# Revit family: Door-Exterior_Interior-Simpson-Sash-Three_Quarter-Half_Arch_Glass-Single
name_source: partatom
category: Doors
revit_build: Autodesk Revit Architecture 2012 (Build: 20110916_2132(x64)
units: mm (PartAtom-declared; Revit-internal decimal feet)

## types (231) — shared parameters
Assembly Code = B2030230
Bottom Panel Height = 0' - 11 5/8"
Bottom Rail Height = 0' - 8 13/16"
Construction Type = Wood
Frame = Wood - Simpson Doors - Douglas Fir
Frame Projection Ext. = 0' - 1"
Frame Projection Int. = 0' - 1"
Frame Type = Frame : Standard
Frame Width = 0' - 3"
Function = Exterior
Glass = Glass - Simpson Doors - Clear
Glass Options = http://simpsondoor.com
Horizontal Outside Muntin = No
Innerbond Double Hip-Raised Panel = Yes
Manufacturer = Simpsons Door Company
Middle Rail Height = 0' - 6 1/2"
Muntin Width = 0' - 0 1/2"
Ovolo Construction = Yes
Panel = Wood - Simpson Doors - Douglas Fir
Panel Divider Width = 0' - 3 1/2"
Panel Stile Width = 0' - 5"
Product Documentation Link = http://www.simpsondoor.com
Product Page URL = http://www.simpsondoor.com
Thickness = 0' - 1 3/4"
Thickness Note = comes in 1 3/4" and 2 1/4" Thickness. Default is set to 1 3/4"
Top Rail Height = 0' - 4 1/32"
URL = http://www.simpsondoor.com
UltraBlock Note = This Door Comes with The Option of UltraBlock Technology. It is Turn On as a Default
UltraBlock Option = Yes
Vertical Outside Muntin = No
Wall Closure = By host
WaterBarrier Note = This Door Comes with The Option of WaterBarrier with UltraBlock Technology. It is Turn Off as a Default
WaterBarrier with UltraBlock Technology = No
Wood Species = http://simpsondoor.com
Wood Species Note = Available in Any Wood Species
zero-valued in all types: Number of Panel Dividers

## per-type parameters (varying)
| type | Description | Height | Model | Number of Horizontal Muntins | Number of Vertical Muntins | Rough Height | Rough Width | Width |
| 37604-37614 Thermal French 30x80 Ovolo Flat Panel | Thermal French SDL - Four Lite - Single Panel | 6' - 8" | 37604-37614 | 1 | 1 | 6' - 10" | 2' - 10" | 2' - 6" |
| 37604-37614 Thermal French 30x84 Ovolo Flat Panel | Thermal French SDL - Four Lite - Single Panel | 7' - 0" | 37604-37614 | 1 | 1 | 7' - 2" | 2' - 10" | 2' - 6" |
| 37604-37614 Thermal French 30x96 Ovolo Flat Panel | Thermal French SDL - Four Lite - Single Panel | 8' - 0" | 37604-37614 | 1 | 1 | 8' - 2" | 2' - 10" | 2' - 6" |
| 37604-37614 Thermal French 32x80 Ovolo Flat Panel | Thermal French SDL - Four Lite - Single Panel | 6' - 8" | 37604-37614 | 1 | 1 | 6' - 10" | 3' - 0" | 2' - 8" |
| 37604-37614 Thermal French 32x84 Ovolo Flat Panel | Thermal French SDL - Four Lite - Single Panel | 7' - 0" | 37604-37614 | 1 | 1 | 7' - 2" | 3' - 0" | 2' - 8" |
| 37604-37614 Thermal French 32x96 Ovolo Flat Panel | Thermal French SDL - Four Lite - Single Panel | 8' - 0" | 37604-37614 | 1 | 1 | 8' - 2" | 3' - 0" | 2' - 8" |
| 37604-37614 Thermal French 34x80 Ovolo Flat Panel | Thermal French SDL - Four Lite - Single Panel | 6' - 8" | 37604-37614 | 1 | 1 | 6' - 10" | 3' - 2" | 2' - 10" |
| 37604-37614 Thermal French 34x84 Ovolo Flat Panel | Thermal French SDL - Four Lite - Single Panel | 7' - 0" | 37604-37614 | 1 | 1 | 7' - 2" | 3' - 2" | 2' - 10" |
| 37604-37614 Thermal French 34x96 Ovolo Flat Panel | Thermal French SDL - Four Lite - Single Panel | 8' - 0" | 37604-37614 | 1 | 1 | 8' - 2" | 3' - 2" | 2' - 10" |
| 37604-37614 Thermal French 36x80 Ovolo Flat Panel | Thermal French SDL - Four Lite - Single Panel | 6' - 8" | 37604-37614 | 1 | 1 | 6' - 10" | 3' - 4" | 3' - 0" |
| 37604-37614 Thermal French 36x84 Ovolo Flat Panel | Thermal French SDL - Four Lite - Single Panel | 7' - 0" | 37604-37614 | 1 | 1 | 7' - 2" | 3' - 4" | 3' - 0" |
| 37604-37614 Thermal French 36x96 Ovolo Flat Panel | Thermal French SDL - Four Lite - Single Panel | 8' - 0" | 37604-37614 | 1 | 1 | 8' - 2" | 3' - 4" | 3' - 0" |
| 37604-37614 Thermal French 38x80 Ovolo Flat Panel | Thermal French SDL - Four Lite - Single Panel | 6' - 8" | 37604-37614 | 1 | 1 | 6' - 10" | 3' - 6" | 3' - 2" |
| 37604-37614 Thermal French 38x84 Ovolo Flat Panel | Thermal French SDL - Four Lite - Single Panel | 7' - 0" | 37604-37614 | 1 | 1 | 7' - 2" | 3' - 6" | 3' - 2" |
| 37604-37614 Thermal French 38x96 Ovolo Flat Panel | Thermal French SDL - Four Lite - Single Panel | 8' - 0" | 37604-37614 | 1 | 1 | 8' - 2" | 3' - 6" | 3' - 2" |
| 37604-37614 Thermal French 40x80 Ovolo Flat Panel | Thermal French SDL - Four Lite - Single Panel | 6' - 8" | 37604-37614 | 1 | 1 | 6' - 10" | 3' - 8" | 3' - 4" |
| 37604-37614 Thermal French 40x84 Ovolo Flat Panel | Thermal French SDL - Four Lite - Single Panel | 7' - 0" | 37604-37614 | 1 | 1 | 7' - 2" | 3' - 8" | 3' - 4" |
| 37604-37614 Thermal French 40x96 Ovolo Flat Panel | Thermal French SDL - Four Lite - Single Panel | 8' - 0" | 37604-37614 | 1 | 1 | 8' - 2" | 3' - 8" | 3' - 4" |
| 37604-37614 Thermal French 42x80 Ovolo Flat Panel | Thermal French SDL - Four Lite - Single Panel | 6' - 8" | 37604-37614 | 1 | 1 | 6' - 10" | 3' - 10" | 3' - 6" |
| 37604-37614 Thermal French 42x84 Ovolo Flat Panel | Thermal French SDL - Four Lite - Single Panel | 7' - 0" | 37604-37614 | 1 | 1 | 7' - 2" | 3' - 10" | 3' - 6" |
| 37604-37614 Thermal French 42x96 Ovolo Flat Panel | Thermal French SDL - Four Lite - Single Panel | 8' - 0" | 37604-37614 | 1 | 1 | 8' - 2" | 3' - 10" | 3' - 6" |
| 37626-37636 Thermal French 30x80 Ovolo Flat Panel | Thermal French SDL - Six Lite - Single Panel | 6' - 8" | 37626-37636 | 2 | 1 | 6' - 10" | 2' - 10" | 2' - 6" |
| 37626-37636 Thermal French 30x84 Ovolo Flat Panel | Thermal French SDL - Six Lite - Single Panel | 7' - 0" | 37626-37636 | 2 | 1 | 7' - 2" | 2' - 10" | 2' - 6" |
| 37626-37636 Thermal French 30x96 Ovolo Flat Panel | Thermal French SDL - Six Lite - Single Panel | 8' - 0" | 37626-37636 | 2 | 1 | 8' - 2" | 2' - 10" | 2' - 6" |
| 37626-37636 Thermal French 32x80 Ovolo Flat Panel | Thermal French SDL - Six Lite - Single Panel | 6' - 8" | 37626-37636 | 2 | 1 | 6' - 10" | 3' - 0" | 2' - 8" |
| 37626-37636 Thermal French 32x84 Ovolo Flat Panel | Thermal French SDL - Six Lite - Single Panel | 7' - 0" | 37626-37636 | 2 | 1 | 7' - 2" | 3' - 0" | 2' - 8" |
| 37626-37636 Thermal French 32x96 Ovolo Flat Panel | Thermal French SDL - Six Lite - Single Panel | 8' - 0" | 37626-37636 | 2 | 1 | 8' - 2" | 3' - 0" | 2' - 8" |
| 37626-37636 Thermal French 34x80 Ovolo Flat Panel | Thermal French SDL - Six Lite - Single Panel | 6' - 8" | 37626-37636 | 2 | 1 | 6' - 10" | 3' - 2" | 2' - 10" |
| 37626-37636 Thermal French 34x84 Ovolo Flat Panel | Thermal French SDL - Six Lite - Single Panel | 7' - 0" | 37626-37636 | 2 | 1 | 7' - 2" | 3' - 2" | 2' - 10" |
| 37626-37636 Thermal French 34x96 Ovolo Flat Panel | Thermal French SDL - Six Lite - Single Panel | 8' - 0" | 37626-37636 | 2 | 1 | 8' - 2" | 3' - 2" | 2' - 10" |
| 37626-37636 Thermal French 36x80 Ovolo Flat Panel | Thermal French SDL - Six Lite - Single Panel | 6' - 8" | 37626-37636 | 2 | 1 | 6' - 10" | 3' - 4" | 3' - 0" |
| 37626-37636 Thermal French 36x84 Ovolo Flat Panel | Thermal French SDL - Six Lite - Single Panel | 7' - 0" | 37626-37636 | 2 | 1 | 7' - 2" | 3' - 4" | 3' - 0" |
| 37626-37636 Thermal French 36x96 Ovolo Flat Panel | Thermal French SDL - Six Lite - Single Panel | 8' - 0" | 37626-37636 | 2 | 1 | 8' - 2" | 3' - 4" | 3' - 0" |
| 37626-37636 Thermal French 38x80 Ovolo Flat Panel | Thermal French SDL - Six Lite - Single Panel | 6' - 8" | 37626-37636 | 2 | 1 | 6' - 10" | 3' - 6" | 3' - 2" |
| 37626-37636 Thermal French 38x84 Ovolo Flat Panel | Thermal French SDL - Six Lite - Single Panel | 7' - 0" | 37626-37636 | 2 | 1 | 7' - 2" | 3' - 6" | 3' - 2" |
| 37626-37636 Thermal French 38x96 Ovolo Flat Panel | Thermal French SDL - Six Lite - Single Panel | 8' - 0" | 37626-37636 | 2 | 1 | 8' - 2" | 3' - 6" | 3' - 2" |
| 37626-37636 Thermal French 40x80 Ovolo Flat Panel | Thermal French SDL - Six Lite - Single Panel | 6' - 8" | 37626-37636 | 2 | 1 | 6' - 10" | 3' - 8" | 3' - 4" |
| 37626-37636 Thermal French 40x84 Ovolo Flat Panel | Thermal French SDL - Six Lite - Single Panel | 7' - 0" | 37626-37636 | 2 | 1 | 7' - 2" | 3' - 8" | 3' - 4" |
| 37626-37636 Thermal French 40x96 Ovolo Flat Panel | Thermal French SDL - Six Lite - Single Panel | 8' - 0" | 37626-37636 | 2 | 1 | 8' - 2" | 3' - 8" | 3' - 4" |
| 37626-37636 Thermal French 42x80 Ovolo Flat Panel | Thermal French SDL - Six Lite - Single Panel | 6' - 8" | 37626-37636 | 2 | 1 | 6' - 10" | 3' - 10" | 3' - 6" |
| 37626-37636 Thermal French 42x84 Ovolo Flat Panel | Thermal French SDL - Six Lite - Single Panel | 7' - 0" | 37626-37636 | 2 | 1 | 7' - 2" | 3' - 10" | 3' - 6" |
| 37626-37636 Thermal French 42x96 Ovolo Flat Panel | Thermal French SDL - Six Lite - Single Panel | 8' - 0" | 37626-37636 | 2 | 1 | 8' - 2" | 3' - 10" | 3' - 6" |
| 37628-37638 Thermal French 30x80 Ovolo Flat Panel | Thermal French SDL - Eight Lite - Single Panel | 6' - 8" | 37628-37638 | 3 | 1 | 6' - 10" | 2' - 10" | 2' - 6" |
| 37628-37638 Thermal French 30x84 Ovolo Flat Panel | Thermal French SDL - Eight Lite - Single Panel | 7' - 0" | 37628-37638 | 3 | 1 | 7' - 2" | 2' - 10" | 2' - 6" |
| 37628-37638 Thermal French 30x96 Ovolo Flat Panel | Thermal French SDL - Eight Lite - Single Panel | 8' - 0" | 37628-37638 | 3 | 1 | 8' - 2" | 2' - 10" | 2' - 6" |
| 37628-37638 Thermal French 32x80 Ovolo Flat Panel | Thermal French SDL - Eight Lite - Single Panel | 6' - 8" | 37628-37638 | 3 | 1 | 6' - 10" | 3' - 0" | 2' - 8" |
| 37628-37638 Thermal French 32x84 Ovolo Flat Panel | Thermal French SDL - Eight Lite - Single Panel | 7' - 0" | 37628-37638 | 3 | 1 | 7' - 2" | 3' - 0" | 2' - 8" |
| 37628-37638 Thermal French 32x96 Ovolo Flat Panel | Thermal French SDL - Eight Lite - Single Panel | 8' - 0" | 37628-37638 | 3 | 1 | 8' - 2" | 3' - 0" | 2' - 8" |
| 37628-37638 Thermal French 34x80 Ovolo Flat Panel | Thermal French SDL - Eight Lite - Single Panel | 6' - 8" | 37628-37638 | 3 | 1 | 6' - 10" | 3' - 2" | 2' - 10" |
| 37628-37638 Thermal French 34x84 Ovolo Flat Panel | Thermal French SDL - Eight Lite - Single Panel | 7' - 0" | 37628-37638 | 3 | 1 | 7' - 2" | 3' - 2" | 2' - 10" |
| 37628-37638 Thermal French 34x96 Ovolo Flat Panel | Thermal French SDL - Eight Lite - Single Panel | 8' - 0" | 37628-37638 | 3 | 1 | 8' - 2" | 3' - 2" | 2' - 10" |
| 37628-37638 Thermal French 36x80 Ovolo Flat Panel | Thermal French SDL - Eight Lite - Single Panel | 6' - 8" | 37628-37638 | 3 | 1 | 6' - 10" | 3' - 4" | 3' - 0" |
| 37628-37638 Thermal French 36x84 Ovolo Flat Panel | Thermal French SDL - Eight Lite - Single Panel | 7' - 0" | 37628-37638 | 3 | 1 | 7' - 2" | 3' - 4" | 3' - 0" |
| 37628-37638 Thermal French 36x96 Ovolo Flat Panel | Thermal French SDL - Eight Lite - Single Panel | 8' - 0" | 37628-37638 | 3 | 1 | 8' - 2" | 3' - 4" | 3' - 0" |
| 37628-37638 Thermal French 38x80 Ovolo Flat Panel | Thermal French SDL - Eight Lite - Single Panel | 6' - 8" | 37628-37638 | 3 | 1 | 6' - 10" | 3' - 6" | 3' - 2" |
| 37628-37638 Thermal French 38x84 Ovolo Flat Panel | Thermal French SDL - Eight Lite - Single Panel | 7' - 0" | 37628-37638 | 3 | 1 | 7' - 2" | 3' - 6" | 3' - 2" |
| 37628-37638 Thermal French 38x96 Ovolo Flat Panel | Thermal French SDL - Eight Lite - Single Panel | 8' - 0" | 37628-37638 | 3 | 1 | 8' - 2" | 3' - 6" | 3' - 2" |
| 37628-37638 Thermal French 40x80 Ovolo Flat Panel | Thermal French SDL - Eight Lite - Single Panel | 6' - 8" | 37628-37638 | 3 | 1 | 6' - 10" | 3' - 8" | 3' - 4" |
| 37628-37638 Thermal French 40x84 Ovolo Flat Panel | Thermal French SDL - Eight Lite - Single Panel | 7' - 0" | 37628-37638 | 3 | 1 | 7' - 2" | 3' - 8" | 3' - 4" |
| 37628-37638 Thermal French 40x96 Ovolo Flat Panel | Thermal French SDL - Eight Lite - Single Panel | 8' - 0" | 37628-37638 | 3 | 1 | 8' - 2" | 3' - 8" | 3' - 4" |
| 37628-37638 Thermal French 42x80 Ovolo Flat Panel | Thermal French SDL - Eight Lite - Single Panel | 6' - 8" | 37628-37638 | 3 | 1 | 6' - 10" | 3' - 10" | 3' - 6" |
| 37628-37638 Thermal French 42x84 Ovolo Flat Panel | Thermal French SDL - Eight Lite - Single Panel | 7' - 0" | 37628-37638 | 3 | 1 | 7' - 2" | 3' - 10" | 3' - 6" |
| 37628-37638 Thermal French 42x96 Ovolo Flat Panel | Thermal French SDL - Eight Lite - Single Panel | 8' - 0" | 37628-37638 | 3 | 1 | 8' - 2" | 3' - 10" | 3' - 6" |
| 544-554 Exterior French & Sash 30x80 Ovolo Flat Panel | Exterior French - Four Lite - Single Panel | 6' - 8" | 544-554 | 1 | 1 | 6' - 10" | 2' - 10" | 2' - 6" |
| 544-554 Exterior French & Sash 30x84 Ovolo Flat Panel | Exterior French - Four Lite - Single Panel | 7' - 0" | 544-554 | 1 | 1 | 7' - 2" | 2' - 10" | 2' - 6" |
| 544-554 Exterior French & Sash 30x96 Ovolo Flat Panel | Exterior French - Four Lite - Single Panel | 8' - 0" | 544-554 | 1 | 1 | 8' - 2" | 2' - 10" | 2' - 6" |
| 544-554 Exterior French & Sash 32x80 Ovolo Flat Panel | Exterior French - Four Lite - Single Panel | 6' - 8" | 544-554 | 1 | 1 | 6' - 10" | 3' - 0" | 2' - 8" |
| 544-554 Exterior French & Sash 32x84 Ovolo Flat Panel | Exterior French - Four Lite - Single Panel | 7' - 0" | 544-554 | 1 | 1 | 7' - 2" | 3' - 0" | 2' - 8" |
| 544-554 Exterior French & Sash 32x96 Ovolo Flat Panel | Exterior French - Four Lite - Single Panel | 8' - 0" | 544-554 | 1 | 1 | 8' - 2" | 3' - 0" | 2' - 8" |
| 544-554 Exterior French & Sash 34x80 Ovolo Flat Panel | Exterior French - Four Lite - Single Panel | 6' - 8" | 544-554 | 1 | 1 | 6' - 10" | 3' - 2" | 2' - 10" |
| 544-554 Exterior French & Sash 34x84 Ovolo Flat Panel | Exterior French - Four Lite - Single Panel | 7' - 0" | 544-554 | 1 | 1 | 7' - 2" | 3' - 2" | 2' - 10" |
| 544-554 Exterior French & Sash 34x96 Ovolo Flat Panel | Exterior French - Four Lite - Single Panel | 8' - 0" | 544-554 | 1 | 1 | 8' - 2" | 3' - 2" | 2' - 10" |
| 544-554 Exterior French & Sash 36x80 Ovolo Flat Panel | Exterior French - Four Lite - Single Panel | 6' - 8" | 544-554 | 1 | 1 | 6' - 10" | 3' - 4" | 3' - 0" |
| 544-554 Exterior French & Sash 36x84 Ovolo Flat Panel | Exterior French - Four Lite - Single Panel | 7' - 0" | 544-554 | 1 | 1 | 7' - 2" | 3' - 4" | 3' - 0" |
| 544-554 Exterior French & Sash 36x96 Ovolo Flat Panel | Exterior French - Four Lite - Single Panel | 8' - 0" | 544-554 | 1 | 1 | 8' - 2" | 3' - 4" | 3' - 0" |
| 544-554 Exterior French & Sash 38x80 Ovolo Flat Panel | Exterior French - Four Lite - Single Panel | 6' - 8" | 544-554 | 1 | 1 | 6' - 10" | 3' - 6" | 3' - 2" |
| 544-554 Exterior French & Sash 38x84 Ovolo Flat Panel | Exterior French - Four Lite - Single Panel | 7' - 0" | 544-554 | 1 | 1 | 7' - 2" | 3' - 6" | 3' - 2" |
| 544-554 Exterior French & Sash 38x96 Ovolo Flat Panel | Exterior French - Four Lite - Single Panel | 8' - 0" | 544-554 | 1 | 1 | 8' - 2" | 3' - 6" | 3' - 2" |
| 544-554 Exterior French & Sash 40x80 Ovolo Flat Panel | Exterior French - Four Lite - Single Panel | 6' - 8" | 544-554 | 1 | 1 | 6' - 10" | 3' - 8" | 3' - 4" |
| 544-554 Exterior French & Sash 40x84 Ovolo Flat Panel | Exterior French - Four Lite - Single Panel | 7' - 0" | 544-554 | 1 | 1 | 7' - 2" | 3' - 8" | 3' - 4" |
| 544-554 Exterior French & Sash 40x96 Ovolo Flat Panel | Exterior French - Four Lite - Single Panel | 8' - 0" | 544-554 | 1 | 1 | 8' - 2" | 3' - 8" | 3' - 4" |
| 544-554 Exterior French & Sash 42x80 Ovolo Flat Panel | Exterior French - Four Lite - Single Panel | 6' - 8" | 544-554 | 1 | 1 | 6' - 10" | 3' - 10" | 3' - 6" |
| 544-554 Exterior French & Sash 42x84 Ovolo Flat Panel | Exterior French - Four Lite - Single Panel | 7' - 0" | 544-554 | 1 | 1 | 7' - 2" | 3' - 10" | 3' - 6" |
| 544-554 Exterior French & Sash 42x96 Ovolo Flat Panel | Exterior French - Four Lite - Single Panel | 8' - 0" | 544-554 | 1 | 1 | 8' - 2" | 3' - 10" | 3' - 6" |
| 556-576 Exterior French & Sash 30x80 Ovolo Flat Panel | Exterior French - Six Lite - Single Panel | 6' - 8" | 556-576 | 2 | 1 | 6' - 10" | 2' - 10" | 2' - 6" |
| 556-576 Exterior French & Sash 30x84 Ovolo Flat Panel | Exterior French - Six Lite - Single Panel | 7' - 0" | 556-576 | 2 | 1 | 7' - 2" | 2' - 10" | 2' - 6" |
| 556-576 Exterior French & Sash 30x96 Ovolo Flat Panel | Exterior French - Six Lite - Single Panel | 8' - 0" | 556-576 | 2 | 1 | 8' - 2" | 2' - 10" | 2' - 6" |
| 556-576 Exterior French & Sash 32x80 Ovolo Flat Panel | Exterior French - Six Lite - Single Panel | 6' - 8" | 556-576 | 2 | 1 | 6' - 10" | 3' - 0" | 2' - 8" |
| 556-576 Exterior French & Sash 32x84 Ovolo Flat Panel | Exterior French - Six Lite - Single Panel | 7' - 0" | 556-576 | 2 | 1 | 7' - 2" | 3' - 0" | 2' - 8" |
| 556-576 Exterior French & Sash 32x96 Ovolo Flat Panel | Exterior French - Six Lite - Single Panel | 8' - 0" | 556-576 | 2 | 1 | 8' - 2" | 3' - 0" | 2' - 8" |
| 556-576 Exterior French & Sash 34x80 Ovolo Flat Panel | Exterior French - Six Lite - Single Panel | 6' - 8" | 556-576 | 2 | 1 | 6' - 10" | 3' - 2" | 2' - 10" |
| 556-576 Exterior French & Sash 34x84 Ovolo Flat Panel | Exterior French - Six Lite - Single Panel | 7' - 0" | 556-576 | 2 | 1 | 7' - 2" | 3' - 2" | 2' - 10" |
| 556-576 Exterior French & Sash 34x96 Ovolo Flat Panel | Exterior French - Six Lite - Single Panel | 8' - 0" | 556-576 | 2 | 1 | 8' - 2" | 3' - 2" | 2' - 10" |
| 556-576 Exterior French & Sash 36x80 Ovolo Flat Panel | Exterior French - Six Lite - Single Panel | 6' - 8" | 556-576 | 2 | 1 | 6' - 10" | 3' - 4" | 3' - 0" |
| 556-576 Exterior French & Sash 36x84 Ovolo Flat Panel | Exterior French - Six Lite - Single Panel | 7' - 0" | 556-576 | 2 | 1 | 7' - 2" | 3' - 4" | 3' - 0" |
| 556-576 Exterior French & Sash 36x96 Ovolo Flat Panel | Exterior French - Six Lite - Single Panel | 8' - 0" | 556-576 | 2 | 1 | 8' - 2" | 3' - 4" | 3' - 0" |
| 556-576 Exterior French & Sash 38x80 Ovolo Flat Panel | Exterior French - Six Lite - Single Panel | 6' - 8" | 556-576 | 2 | 1 | 6' - 10" | 3' - 6" | 3' - 2" |
| 556-576 Exterior French & Sash 38x84 Ovolo Flat Panel | Exterior French - Six Lite - Single Panel | 7' - 0" | 556-576 | 2 | 1 | 7' - 2" | 3' - 6" | 3' - 2" |
| 556-576 Exterior French & Sash 38x96 Ovolo Flat Panel | Exterior French - Six Lite - Single Panel | 8' - 0" | 556-576 | 2 | 1 | 8' - 2" | 3' - 6" | 3' - 2" |
| 556-576 Exterior French & Sash 40x80 Ovolo Flat Panel | Exterior French - Six Lite - Single Panel | 6' - 8" | 556-576 | 2 | 1 | 6' - 10" | 3' - 8" | 3' - 4" |
| 556-576 Exterior French & Sash 40x84 Ovolo Flat Panel | Exterior French - Six Lite - Single Panel | 7' - 0" | 556-576 | 2 | 1 | 7' - 2" | 3' - 8" | 3' - 4" |
| 556-576 Exterior French & Sash 40x96 Ovolo Flat Panel | Exterior French - Six Lite - Single Panel | 8' - 0" | 556-576 | 2 | 1 | 8' - 2" | 3' - 8" | 3' - 4" |
| 556-576 Exterior French & Sash 42x80 Ovolo Flat Panel | Exterior French - Six Lite - Single Panel | 6' - 8" | 556-576 | 2 | 1 | 6' - 10" | 3' - 10" | 3' - 6" |
| 556-576 Exterior French & Sash 42x84 Ovolo Flat Panel | Exterior French - Six Lite - Single Panel | 7' - 0" | 556-576 | 2 | 1 | 7' - 2" | 3' - 10" | 3' - 6" |
| 556-576 Exterior French & Sash 42x96 Ovolo Flat Panel | Exterior French - Six Lite - Single Panel | 8' - 0" | 556-576 | 2 | 1 | 8' - 2" | 3' - 10" | 3' - 6" |
| 561-571 Exterior French & Sash 30x80 Ovolo Flat Panel | Exterior French - Single Lite - Single Panel | 6' - 8" | 561-571 | 0 | 0 | 6' - 10" | 2' - 10" | 2' - 6" |
| 561-571 Exterior French & Sash 30x84 Ovolo Flat Panel | Exterior French - Single Lite - Single Panel | 7' - 0" | 561-571 | 0 | 0 | 7' - 2" | 2' - 10" | 2' - 6" |
| 561-571 Exterior French & Sash 30x96 Ovolo Flat Panel | Exterior French - Single Lite - Single Panel | 8' - 0" | 561-571 | 0 | 0 | 8' - 2" | 2' - 10" | 2' - 6" |
| 561-571 Exterior French & Sash 32x80 Ovolo Flat Panel | Exterior French - Single Lite - Single Panel | 6' - 8" | 561-571 | 0 | 0 | 6' - 10" | 3' - 0" | 2' - 8" |
| 561-571 Exterior French & Sash 32x84 Ovolo Flat Panel | Exterior French - Single Lite - Single Panel | 7' - 0" | 561-571 | 0 | 0 | 7' - 2" | 3' - 0" | 2' - 8" |
| 561-571 Exterior French & Sash 32x96 Ovolo Flat Panel | Exterior French - Single Lite - Single Panel | 8' - 0" | 561-571 | 0 | 0 | 8' - 2" | 3' - 0" | 2' - 8" |
| 561-571 Exterior French & Sash 34x80 Ovolo Flat Panel | Exterior French - Single Lite - Single Panel | 6' - 8" | 561-571 | 0 | 0 | 6' - 10" | 3' - 2" | 2' - 10" |
| 561-571 Exterior French & Sash 34x84 Ovolo Flat Panel | Exterior French - Single Lite - Single Panel | 7' - 0" | 561-571 | 0 | 0 | 7' - 2" | 3' - 2" | 2' - 10" |
| 561-571 Exterior French & Sash 34x96 Ovolo Flat Panel | Exterior French - Single Lite - Single Panel | 8' - 0" | 561-571 | 0 | 0 | 8' - 2" | 3' - 2" | 2' - 10" |
| 561-571 Exterior French & Sash 36x80 Ovolo Flat Panel | Exterior French - Single Lite - Single Panel | 6' - 8" | 561-571 | 0 | 0 | 6' - 10" | 3' - 4" | 3' - 0" |
| 561-571 Exterior French & Sash 36x84 Ovolo Flat Panel | Exterior French - Single Lite - Single Panel | 7' - 0" | 561-571 | 0 | 0 | 7' - 2" | 3' - 4" | 3' - 0" |
| 561-571 Exterior French & Sash 36x96 Ovolo Flat Panel | Exterior French - Single Lite - Single Panel | 8' - 0" | 561-571 | 0 | 0 | 8' - 2" | 3' - 4" | 3' - 0" |
| 561-571 Exterior French & Sash 38x80 Ovolo Flat Panel | Exterior French - Single Lite - Single Panel | 6' - 8" | 561-571 | 0 | 0 | 6' - 10" | 3' - 6" | 3' - 2" |
| 561-571 Exterior French & Sash 38x84 Ovolo Flat Panel | Exterior French - Single Lite - Single Panel | 7' - 0" | 561-571 | 0 | 0 | 7' - 2" | 3' - 6" | 3' - 2" |
| 561-571 Exterior French & Sash 38x96 Ovolo Flat Panel | Exterior French - Single Lite - Single Panel | 8' - 0" | 561-571 | 0 | 0 | 8' - 2" | 3' - 6" | 3' - 2" |
| 561-571 Exterior French & Sash 40x80 Ovolo Flat Panel | Exterior French - Single Lite - Single Panel | 6' - 8" | 561-571 | 0 | 0 | 6' - 10" | 3' - 8" | 3' - 4" |
| 561-571 Exterior French & Sash 40x84 Ovolo Flat Panel | Exterior French - Single Lite - Single Panel | 7' - 0" | 561-571 | 0 | 0 | 7' - 2" | 3' - 8" | 3' - 4" |
| 561-571 Exterior French & Sash 40x96 Ovolo Flat Panel | Exterior French - Single Lite - Single Panel | 8' - 0" | 561-571 | 0 | 0 | 8' - 2" | 3' - 8" | 3' - 4" |
| 561-571 Exterior French & Sash 42x80 Ovolo Flat Panel | Exterior French - Single Lite - Single Panel | 6' - 8" | 561-571 | 0 | 0 | 6' - 10" | 3' - 10" | 3' - 6" |
| 561-571 Exterior French & Sash 42x84 Ovolo Flat Panel | Exterior French - Single Lite - Single Panel | 7' - 0" | 561-571 | 0 | 0 | 7' - 2" | 3' - 10" | 3' - 6" |
| 561-571 Exterior French & Sash 42x96 Ovolo Flat Panel | Exterior French - Single Lite - Single Panel | 8' - 0" | 561-571 | 0 | 0 | 8' - 2" | 3' - 10" | 3' - 6" |
| 568-578 Exterior French & Sash 30x80 Ovolo Flat Panel | Exterior French - Eight Lite - Single Panel | 6' - 8" | 568-578 | 3 | 1 | 6' - 10" | 2' - 10" | 2' - 6" |
| 568-578 Exterior French & Sash 30x84 Ovolo Flat Panel | Exterior French - Eight Lite - Single Panel | 7' - 0" | 568-578 | 3 | 1 | 7' - 2" | 2' - 10" | 2' - 6" |
| 568-578 Exterior French & Sash 30x96 Ovolo Flat Panel | Exterior French - Eight Lite - Single Panel | 8' - 0" | 568-578 | 3 | 1 | 8' - 2" | 2' - 10" | 2' - 6" |
| 568-578 Exterior French & Sash 32x80 Ovolo Flat Panel | Exterior French - Eight Lite - Single Panel | 6' - 8" | 568-578 | 3 | 1 | 6' - 10" | 3' - 0" | 2' - 8" |
| 568-578 Exterior French & Sash 32x84 Ovolo Flat Panel | Exterior French - Eight Lite - Single Panel | 7' - 0" | 568-578 | 3 | 1 | 7' - 2" | 3' - 0" | 2' - 8" |
| 568-578 Exterior French & Sash 32x96 Ovolo Flat Panel | Exterior French - Eight Lite - Single Panel | 8' - 0" | 568-578 | 3 | 1 | 8' - 2" | 3' - 0" | 2' - 8" |
| 568-578 Exterior French & Sash 34x80 Ovolo Flat Panel | Exterior French - Eight Lite - Single Panel | 6' - 8" | 568-578 | 3 | 1 | 6' - 10" | 3' - 2" | 2' - 10" |
| 568-578 Exterior French & Sash 34x84 Ovolo Flat Panel | Exterior French - Eight Lite - Single Panel | 7' - 0" | 568-578 | 3 | 1 | 7' - 2" | 3' - 2" | 2' - 10" |
| 568-578 Exterior French & Sash 34x96 Ovolo Flat Panel | Exterior French - Eight Lite - Single Panel | 8' - 0" | 568-578 | 3 | 1 | 8' - 2" | 3' - 2" | 2' - 10" |
| 568-578 Exterior French & Sash 36x80 Ovolo Flat Panel | Exterior French - Eight Lite - Single Panel | 6' - 8" | 568-578 | 3 | 1 | 6' - 10" | 3' - 4" | 3' - 0" |
| 568-578 Exterior French & Sash 36x84 Ovolo Flat Panel | Exterior French - Eight Lite - Single Panel | 7' - 0" | 568-578 | 3 | 1 | 7' - 2" | 3' - 4" | 3' - 0" |
| 568-578 Exterior French & Sash 36x96 Ovolo Flat Panel | Exterior French - Eight Lite - Single Panel | 8' - 0" | 568-578 | 3 | 1 | 8' - 2" | 3' - 4" | 3' - 0" |
| 568-578 Exterior French & Sash 38x80 Ovolo Flat Panel | Exterior French - Eight Lite - Single Panel | 6' - 8" | 568-578 | 3 | 1 | 6' - 10" | 3' - 6" | 3' - 2" |
| 568-578 Exterior French & Sash 38x84 Ovolo Flat Panel | Exterior French - Eight Lite - Single Panel | 7' - 0" | 568-578 | 3 | 1 | 7' - 2" | 3' - 6" | 3' - 2" |
| 568-578 Exterior French & Sash 38x96 Ovolo Flat Panel | Exterior French - Eight Lite - Single Panel | 8' - 0" | 568-578 | 3 | 1 | 8' - 2" | 3' - 6" | 3' - 2" |
| 568-578 Exterior French & Sash 40x80 Ovolo Flat Panel | Exterior French - Eight Lite - Single Panel | 6' - 8" | 568-578 | 3 | 1 | 6' - 10" | 3' - 8" | 3' - 4" |
| 568-578 Exterior French & Sash 40x84 Ovolo Flat Panel | Exterior French - Eight Lite - Single Panel | 7' - 0" | 568-578 | 3 | 1 | 7' - 2" | 3' - 8" | 3' - 4" |
| 568-578 Exterior French & Sash 40x96 Ovolo Flat Panel | Exterior French - Eight Lite - Single Panel | 8' - 0" | 568-578 | 3 | 1 | 8' - 2" | 3' - 8" | 3' - 4" |
| 568-578 Exterior French & Sash 42x80 Ovolo Flat Panel | Exterior French - Eight Lite - Single Panel | 6' - 8" | 568-578 | 3 | 1 | 6' - 10" | 3' - 10" | 3' - 6" |
| 568-578 Exterior French & Sash 42x84 Ovolo Flat Panel | Exterior French - Eight Lite - Single Panel | 7' - 0" | 568-578 | 3 | 1 | 7' - 2" | 3' - 10" | 3' - 6" |
| 568-578 Exterior French & Sash 42x96 Ovolo Flat Panel | Exterior French - Eight Lite - Single Panel | 8' - 0" | 568-578 | 3 | 1 | 8' - 2" | 3' - 10" | 3' - 6" |
| 7604-7614 Thermal French 30x80 Ovolo Flat Panel | Thermal French TDL - Four Lite - Single Panel | 6' - 8" | 7604-7614 | 1 | 1 | 6' - 10" | 2' - 10" | 2' - 6" |
| 7604-7614 Thermal French 30x84 Ovolo Flat Panel | Thermal French TDL - Four Lite - Single Panel | 7' - 0" | 7604-7614 | 1 | 1 | 7' - 2" | 2' - 10" | 2' - 6" |
| 7604-7614 Thermal French 30x96 Ovolo Flat Panel | Thermal French TDL - Four Lite - Single Panel | 8' - 0" | 7604-7614 | 1 | 1 | 8' - 2" | 2' - 10" | 2' - 6" |
| 7604-7614 Thermal French 32x80 Ovolo Flat Panel | Thermal French TDL - Four Lite - Single Panel | 6' - 8" | 7604-7614 | 1 | 1 | 6' - 10" | 3' - 0" | 2' - 8" |
| 7604-7614 Thermal French 32x84 Ovolo Flat Panel | Thermal French TDL - Four Lite - Single Panel | 7' - 0" | 7604-7614 | 1 | 1 | 7' - 2" | 3' - 0" | 2' - 8" |
| 7604-7614 Thermal French 32x96 Ovolo Flat Panel | Thermal French TDL - Four Lite - Single Panel | 8' - 0" | 7604-7614 | 1 | 1 | 8' - 2" | 3' - 0" | 2' - 8" |
| 7604-7614 Thermal French 34x80 Ovolo Flat Panel | Thermal French TDL - Four Lite - Single Panel | 6' - 8" | 7604-7614 | 1 | 1 | 6' - 10" | 3' - 2" | 2' - 10" |
| 7604-7614 Thermal French 34x84 Ovolo Flat Panel | Thermal French TDL - Four Lite - Single Panel | 7' - 0" | 7604-7614 | 1 | 1 | 7' - 2" | 3' - 2" | 2' - 10" |
| 7604-7614 Thermal French 34x96 Ovolo Flat Panel | Thermal French TDL - Four Lite - Single Panel | 8' - 0" | 7604-7614 | 1 | 1 | 8' - 2" | 3' - 2" | 2' - 10" |
| 7604-7614 Thermal French 36x80 Ovolo Flat Panel | Thermal French TDL - Four Lite - Single Panel | 6' - 8" | 7604-7614 | 1 | 1 | 6' - 10" | 3' - 4" | 3' - 0" |
| 7604-7614 Thermal French 36x84 Ovolo Flat Panel | Thermal French TDL - Four Lite - Single Panel | 7' - 0" | 7604-7614 | 1 | 1 | 7' - 2" | 3' - 4" | 3' - 0" |
| 7604-7614 Thermal French 36x96 Ovolo Flat Panel | Thermal French TDL - Four Lite - Single Panel | 8' - 0" | 7604-7614 | 1 | 1 | 8' - 2" | 3' - 4" | 3' - 0" |
| 7604-7614 Thermal French 38x80 Ovolo Flat Panel | Thermal French TDL - Four Lite - Single Panel | 6' - 8" | 7604-7614 | 1 | 1 | 6' - 10" | 3' - 6" | 3' - 2" |
| 7604-7614 Thermal French 38x84 Ovolo Flat Panel | Thermal French TDL - Four Lite - Single Panel | 7' - 0" | 7604-7614 | 1 | 1 | 7' - 2" | 3' - 6" | 3' - 2" |
| 7604-7614 Thermal French 38x96 Ovolo Flat Panel | Thermal French TDL - Four Lite - Single Panel | 8' - 0" | 7604-7614 | 1 | 1 | 8' - 2" | 3' - 6" | 3' - 2" |
| 7604-7614 Thermal French 40x80 Ovolo Flat Panel | Thermal French TDL - Four Lite - Single Panel | 6' - 8" | 7604-7614 | 1 | 1 | 6' - 10" | 3' - 8" | 3' - 4" |
| 7604-7614 Thermal French 40x84 Ovolo Flat Panel | Thermal French TDL - Four Lite - Single Panel | 7' - 0" | 7604-7614 | 1 | 1 | 7' - 2" | 3' - 8" | 3' - 4" |
| 7604-7614 Thermal French 40x96 Ovolo Flat Panel | Thermal French TDL - Four Lite - Single Panel | 8' - 0" | 7604-7614 | 1 | 1 | 8' - 2" | 3' - 8" | 3' - 4" |
| 7604-7614 Thermal French 42x80 Ovolo Flat Panel | Thermal French TDL - Four Lite - Single Panel | 6' - 8" | 7604-7614 | 1 | 1 | 6' - 10" | 3' - 10" | 3' - 6" |
| 7604-7614 Thermal French 42x84 Ovolo Flat Panel | Thermal French TDL - Four Lite - Single Panel | 7' - 0" | 7604-7614 | 1 | 1 | 7' - 2" | 3' - 10" | 3' - 6" |
| 7604-7614 Thermal French 42x96 Ovolo Flat Panel | Thermal French TDL - Four Lite - Single Panel | 8' - 0" | 7604-7614 | 1 | 1 | 8' - 2" | 3' - 10" | 3' - 6" |
| 7621-7631 Thermal French 30x80 Ovolo Flat Panel | Thermal French TDL - Single Lite - Single Panel | 6' - 8" | 7621-7631 | 0 | 0 | 6' - 10" | 2' - 10" | 2' - 6" |
| 7621-7631 Thermal French 30x84 Ovolo Flat Panel | Thermal French TDL - Single Lite - Single Panel | 7' - 0" | 7621-7631 | 0 | 0 | 7' - 2" | 2' - 10" | 2' - 6" |
| 7621-7631 Thermal French 30x96 Ovolo Flat Panel | Thermal French TDL - Single Lite - Single Panel | 8' - 0" | 7621-7631 | 0 | 0 | 8' - 2" | 2' - 10" | 2' - 6" |
| 7621-7631 Thermal French 32x80 Ovolo Flat Panel | Thermal French TDL - Single Lite - Single Panel | 6' - 8" | 7621-7631 | 0 | 0 | 6' - 10" | 3' - 0" | 2' - 8" |
| 7621-7631 Thermal French 32x84 Ovolo Flat Panel | Thermal French TDL - Single Lite - Single Panel | 7' - 0" | 7621-7631 | 0 | 0 | 7' - 2" | 3' - 0" | 2' - 8" |
| 7621-7631 Thermal French 32x96 Ovolo Flat Panel | Thermal French TDL - Single Lite - Single Panel | 8' - 0" | 7621-7631 | 0 | 0 | 8' - 2" | 3' - 0" | 2' - 8" |
| 7621-7631 Thermal French 34x80 Ovolo Flat Panel | Thermal French TDL - Single Lite - Single Panel | 6' - 8" | 7621-7631 | 0 | 0 | 6' - 10" | 3' - 2" | 2' - 10" |
| 7621-7631 Thermal French 34x84 Ovolo Flat Panel | Thermal French TDL - Single Lite - Single Panel | 7' - 0" | 7621-7631 | 0 | 0 | 7' - 2" | 3' - 2" | 2' - 10" |
| 7621-7631 Thermal French 34x96 Ovolo Flat Panel | Thermal French TDL - Single Lite - Single Panel | 8' - 0" | 7621-7631 | 0 | 0 | 8' - 2" | 3' - 2" | 2' - 10" |
| 7621-7631 Thermal French 36x80 Ovolo Flat Panel | Thermal French TDL - Single Lite - Single Panel | 6' - 8" | 7621-7631 | 0 | 0 | 6' - 10" | 3' - 4" | 3' - 0" |
| 7621-7631 Thermal French 36x84 Ovolo Flat Panel | Thermal French TDL - Single Lite - Single Panel | 7' - 0" | 7621-7631 | 0 | 0 | 7' - 2" | 3' - 4" | 3' - 0" |
| 7621-7631 Thermal French 36x96 Ovolo Flat Panel | Thermal French TDL - Single Lite - Single Panel | 8' - 0" | 7621-7631 | 0 | 0 | 8' - 2" | 3' - 4" | 3' - 0" |
| 7621-7631 Thermal French 38x80 Ovolo Flat Panel | Thermal French TDL - Single Lite - Single Panel | 6' - 8" | 7621-7631 | 0 | 0 | 6' - 10" | 3' - 6" | 3' - 2" |
| 7621-7631 Thermal French 38x84 Ovolo Flat Panel | Thermal French TDL - Single Lite - Single Panel | 7' - 0" | 7621-7631 | 0 | 0 | 7' - 2" | 3' - 6" | 3' - 2" |
| 7621-7631 Thermal French 38x96 Ovolo Flat Panel | Thermal French TDL - Single Lite - Single Panel | 8' - 0" | 7621-7631 | 0 | 0 | 8' - 2" | 3' - 6" | 3' - 2" |
| 7621-7631 Thermal French 40x80 Ovolo Flat Panel | Thermal French TDL - Single Lite - Single Panel | 6' - 8" | 7621-7631 | 0 | 0 | 6' - 10" | 3' - 8" | 3' - 4" |
| 7621-7631 Thermal French 40x84 Ovolo Flat Panel | Thermal French TDL - Single Lite - Single Panel | 7' - 0" | 7621-7631 | 0 | 0 | 7' - 2" | 3' - 8" | 3' - 4" |
| 7621-7631 Thermal French 40x96 Ovolo Flat Panel | Thermal French TDL - Single Lite - Single Panel | 8' - 0" | 7621-7631 | 0 | 0 | 8' - 2" | 3' - 8" | 3' - 4" |
| 7621-7631 Thermal French 42x80 Ovolo Flat Panel | Thermal French TDL - Single Lite - Single Panel | 6' - 8" | 7621-7631 | 0 | 0 | 6' - 10" | 3' - 10" | 3' - 6" |
| 7621-7631 Thermal French 42x84 Ovolo Flat Panel | Thermal French TDL - Single Lite - Single Panel | 7' - 0" | 7621-7631 | 0 | 0 | 7' - 2" | 3' - 10" | 3' - 6" |
| 7621-7631 Thermal French 42x96 Ovolo Flat Panel | Thermal French TDL - Single Lite - Single Panel | 8' - 0" | 7621-7631 | 0 | 0 | 8' - 2" | 3' - 10" | 3' - 6" |
| 7626-7636 Thermal French 30x80 Ovolo Flat Panel | Thermal French TDL - Six Lite - Single Panel | 6' - 8" | 7626-7636 | 2 | 1 | 6' - 10" | 2' - 10" | 2' - 6" |
| 7626-7636 Thermal French 30x84 Ovolo Flat Panel | Thermal French TDL - Six Lite - Single Panel | 7' - 0" | 7626-7636 | 2 | 1 | 7' - 2" | 2' - 10" | 2' - 6" |
| 7626-7636 Thermal French 30x96 Ovolo Flat Panel | Thermal French TDL - Six Lite - Single Panel | 8' - 0" | 7626-7636 | 2 | 1 | 8' - 2" | 2' - 10" | 2' - 6" |
| 7626-7636 Thermal French 32x80 Ovolo Flat Panel | Thermal French TDL - Six Lite - Single Panel | 6' - 8" | 7626-7636 | 2 | 1 | 6' - 10" | 3' - 0" | 2' - 8" |
| 7626-7636 Thermal French 32x84 Ovolo Flat Panel | Thermal French TDL - Six Lite - Single Panel | 7' - 0" | 7626-7636 | 2 | 1 | 7' - 2" | 3' - 0" | 2' - 8" |
| 7626-7636 Thermal French 32x96 Ovolo Flat Panel | Thermal French TDL - Six Lite - Single Panel | 8' - 0" | 7626-7636 | 2 | 1 | 8' - 2" | 3' - 0" | 2' - 8" |
| 7626-7636 Thermal French 34x80 Ovolo Flat Panel | Thermal French TDL - Six Lite - Single Panel | 6' - 8" | 7626-7636 | 2 | 1 | 6' - 10" | 3' - 2" | 2' - 10" |
| 7626-7636 Thermal French 34x84 Ovolo Flat Panel | Thermal French TDL - Six Lite - Single Panel | 7' - 0" | 7626-7636 | 2 | 1 | 7' - 2" | 3' - 2" | 2' - 10" |
| 7626-7636 Thermal French 34x96 Ovolo Flat Panel | Thermal French TDL - Six Lite - Single Panel | 8' - 0" | 7626-7636 | 2 | 1 | 8' - 2" | 3' - 2" | 2' - 10" |
| 7626-7636 Thermal French 36x80 Ovolo Flat Panel | Thermal French TDL - Six Lite - Single Panel | 6' - 8" | 7626-7636 | 2 | 1 | 6' - 10" | 3' - 4" | 3' - 0" |
| 7626-7636 Thermal French 36x84 Ovolo Flat Panel | Thermal French TDL - Six Lite - Single Panel | 7' - 0" | 7626-7636 | 2 | 1 | 7' - 2" | 3' - 4" | 3' - 0" |
| 7626-7636 Thermal French 36x96 Ovolo Flat Panel | Thermal French TDL - Six Lite - Single Panel | 8' - 0" | 7626-7636 | 2 | 1 | 8' - 2" | 3' - 4" | 3' - 0" |
| 7626-7636 Thermal French 38x80 Ovolo Flat Panel | Thermal French TDL - Six Lite - Single Panel | 6' - 8" | 7626-7636 | 2 | 1 | 6' - 10" | 3' - 6" | 3' - 2" |
| 7626-7636 Thermal French 38x84 Ovolo Flat Panel | Thermal French TDL - Six Lite - Single Panel | 7' - 0" | 7626-7636 | 2 | 1 | 7' - 2" | 3' - 6" | 3' - 2" |
| 7626-7636 Thermal French 38x96 Ovolo Flat Panel | Thermal French TDL - Six Lite - Single Panel | 8' - 0" | 7626-7636 | 2 | 1 | 8' - 2" | 3' - 6" | 3' - 2" |
| 7626-7636 Thermal French 40x80 Ovolo Flat Panel | Thermal French TDL - Six Lite - Single Panel | 6' - 8" | 7626-7636 | 2 | 1 | 6' - 10" | 3' - 8" | 3' - 4" |
| 7626-7636 Thermal French 40x84 Ovolo Flat Panel | Thermal French TDL - Six Lite - Single Panel | 7' - 0" | 7626-7636 | 2 | 1 | 7' - 2" | 3' - 8" | 3' - 4" |
| 7626-7636 Thermal French 40x96 Ovolo Flat Panel | Thermal French TDL - Six Lite - Single Panel | 8' - 0" | 7626-7636 | 2 | 1 | 8' - 2" | 3' - 8" | 3' - 4" |
| 7626-7636 Thermal French 42x80 Ovolo Flat Panel | Thermal French TDL - Six Lite - Single Panel | 6' - 8" | 7626-7636 | 2 | 1 | 6' - 10" | 3' - 10" | 3' - 6" |
| 7626-7636 Thermal French 42x84 Ovolo Flat Panel | Thermal French TDL - Six Lite - Single Panel | 7' - 0" | 7626-7636 | 2 | 1 | 7' - 2" | 3' - 10" | 3' - 6" |
| 7626-7636 Thermal French 42x96 Ovolo Flat Panel | Thermal French TDL - Six Lite - Single Panel | 8' - 0" | 7626-7636 | 2 | 1 | 8' - 2" | 3' - 10" | 3' - 6" |
| 7628-7638 Thermal French 30x80 Ovolo Flat Panel | Thermal French TDL - Eight Lite - Single Panel | 6' - 8" | 7628-7638 | 3 | 1 | 6' - 10" | 2' - 10" | 2' - 6" |
| 7628-7638 Thermal French 30x84 Ovolo Flat Panel | Thermal French TDL - Eight Lite - Single Panel | 7' - 0" | 7628-7638 | 3 | 1 | 7' - 2" | 2' - 10" | 2' - 6" |
| 7628-7638 Thermal French 30x96 Ovolo Flat Panel | Thermal French TDL - Eight Lite - Single Panel | 8' - 0" | 7628-7638 | 3 | 1 | 8' - 2" | 2' - 10" | 2' - 6" |
| 7628-7638 Thermal French 32x80 Ovolo Flat Panel | Thermal French TDL - Eight Lite - Single Panel | 6' - 8" | 7628-7638 | 3 | 1 | 6' - 10" | 3' - 0" | 2' - 8" |
| 7628-7638 Thermal French 32x84 Ovolo Flat Panel | Thermal French TDL - Eight Lite - Single Panel | 7' - 0" | 7628-7638 | 3 | 1 | 7' - 2" | 3' - 0" | 2' - 8" |
| 7628-7638 Thermal French 32x96 Ovolo Flat Panel | Thermal French TDL - Eight Lite - Single Panel | 8' - 0" | 7628-7638 | 3 | 1 | 8' - 2" | 3' - 0" | 2' - 8" |
| 7628-7638 Thermal French 34x80 Ovolo Flat Panel | Thermal French TDL - Eight Lite - Single Panel | 6' - 8" | 7628-7638 | 3 | 1 | 6' - 10" | 3' - 2" | 2' - 10" |
| 7628-7638 Thermal French 34x84 Ovolo Flat Panel | Thermal French TDL - Eight Lite - Single Panel | 7' - 0" | 7628-7638 | 3 | 1 | 7' - 2" | 3' - 2" | 2' - 10" |
| 7628-7638 Thermal French 34x96 Ovolo Flat Panel | Thermal French TDL - Eight Lite - Single Panel | 8' - 0" | 7628-7638 | 3 | 1 | 8' - 2" | 3' - 2" | 2' - 10" |
| 7628-7638 Thermal French 36x80 Ovolo Flat Panel | Thermal French TDL - Eight Lite - Single Panel | 6' - 8" | 7628-7638 | 3 | 1 | 6' - 10" | 3' - 4" | 3' - 0" |
| 7628-7638 Thermal French 36x84 Ovolo Flat Panel | Thermal French TDL - Eight Lite - Single Panel | 7' - 0" | 7628-7638 | 3 | 1 | 7' - 2" | 3' - 4" | 3' - 0" |
| 7628-7638 Thermal French 36x96 Ovolo Flat Panel | Thermal French TDL - Eight Lite - Single Panel | 8' - 0" | 7628-7638 | 3 | 1 | 8' - 2" | 3' - 4" | 3' - 0" |
| 7628-7638 Thermal French 38x80 Ovolo Flat Panel | Thermal French TDL - Eight Lite - Single Panel | 6' - 8" | 7628-7638 | 3 | 1 | 6' - 10" | 3' - 6" | 3' - 2" |
| 7628-7638 Thermal French 38x84 Ovolo Flat Panel | Thermal French TDL - Eight Lite - Single Panel | 7' - 0" | 7628-7638 | 3 | 1 | 7' - 2" | 3' - 6" | 3' - 2" |
| 7628-7638 Thermal French 38x96 Ovolo Flat Panel | Thermal French TDL - Eight Lite - Single Panel | 8' - 0" | 7628-7638 | 3 | 1 | 8' - 2" | 3' - 6" | 3' - 2" |
| 7628-7638 Thermal French 40x80 Ovolo Flat Panel | Thermal French TDL - Eight Lite - Single Panel | 6' - 8" | 7628-7638 | 3 | 1 | 6' - 10" | 3' - 8" | 3' - 4" |
| 7628-7638 Thermal French 40x84 Ovolo Flat Panel | Thermal French TDL - Eight Lite - Single Panel | 7' - 0" | 7628-7638 | 3 | 1 | 7' - 2" | 3' - 8" | 3' - 4" |
| 7628-7638 Thermal French 40x96 Ovolo Flat Panel | Thermal French TDL - Eight Lite - Single Panel | 8' - 0" | 7628-7638 | 3 | 1 | 8' - 2" | 3' - 8" | 3' - 4" |
| 7628-7638 Thermal French 42x80 Ovolo Flat Panel | Thermal French TDL - Eight Lite - Single Panel | 6' - 8" | 7628-7638 | 3 | 1 | 6' - 10" | 3' - 10" | 3' - 6" |
| 7628-7638 Thermal French 42x84 Ovolo Flat Panel | Thermal French TDL - Eight Lite - Single Panel | 7' - 0" | 7628-7638 | 3 | 1 | 7' - 2" | 3' - 10" | 3' - 6" |
| 7628-7638 Thermal French 42x96 Ovolo Flat Panel | Thermal French TDL - Eight Lite - Single Panel | 8' - 0" | 7628-7638 | 3 | 1 | 8' - 2" | 3' - 10" | 3' - 6" |

## geometry (parser evidence)
native form markers: Blend x4, Sweep x24
no freeform markers — native parametric forms only
